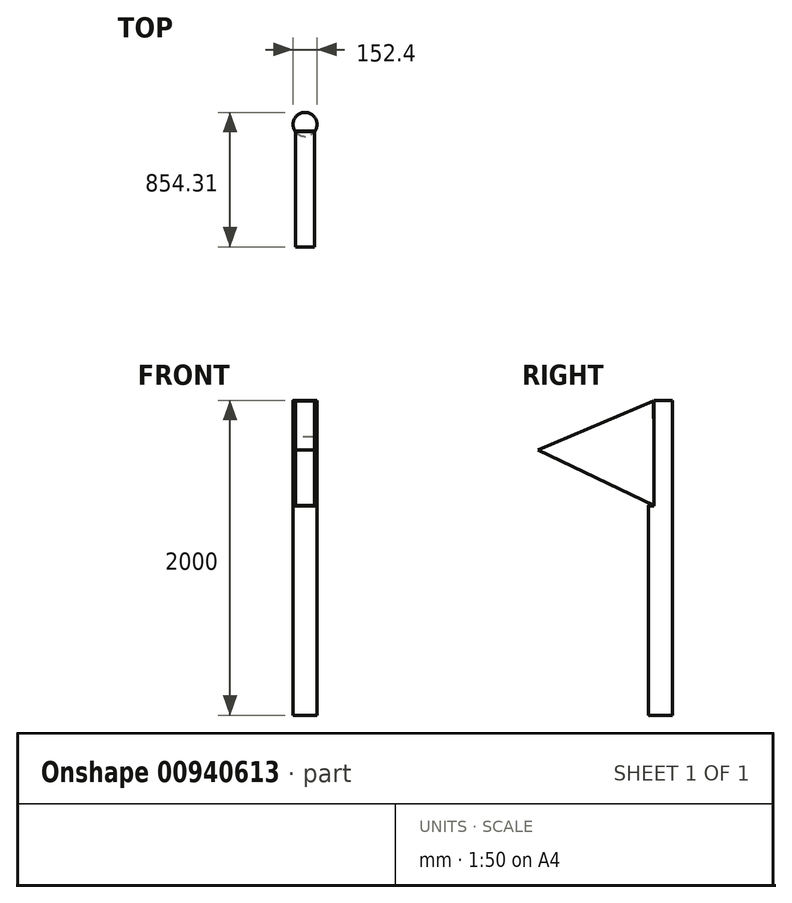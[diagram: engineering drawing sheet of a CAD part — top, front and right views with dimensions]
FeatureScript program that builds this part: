
annotation { "Feature Type Name" : "Feature", "Feature Type Description" : "" }
export const myFeature = defineFeature(function(context is Context, id is Id, definition is map)
    precondition{}
    {
        {
            var Q0;
            Q0=qCreatedBy(makeId("Top.planeOp"),FACE);
            var sketch = newSketch(context, id + "F0", { "sketchPlane" : qUnion([Q0])});
            skCircle(sketch, "E0", {"center": v(0, 0) * mm, "radius": 76.2 * mm});
            skSolve(sketch);
        }
        {
            var Q0;
            Q0=makeQuery(id+"F0.imprint","IMPRINT",FACE,{"disambiguationData":[TD([[makeQuery(id+"F0.imprint","IMPRINT",EDGE,{"derivedFrom":sQuery(id+"F0.wireOp",EDGE,"E0")}),1.0]])]});
            extrude(context, id + "F1", {"entities" : qUnion([Q0]), "depth" : 2000 * mm, "offsetDistance" : 25 * mm});
        }
        {
            var Q0;
            Q0=makeQuery(id+"F1.opExtrude","CAP_FACE",FACE,{"disambiguationData":[OSD([sQuery(id+"F0.wireOp",EDGE,"E0")])],"isStart":false});
            var sketch = newSketch(context, id + "F2", { "sketchPlane" : qUnion([Q0])});
            skLineSegment(sketch, "E1.bottom", {"start": v(-76.2, -42.65) * mm, "end": v(76.2, -42.65) * mm});
            skLineSegment(sketch, "E1.top", {"start": v(-76.2, -102.65) * mm, "end": v(76.2, -102.65) * mm});
            skLineSegment(sketch, "E1.left", {"start": v(-76.2, -42.65) * mm, "end": v(-76.2, -102.65) * mm});
            skLineSegment(sketch, "E1.right", {"start": v(76.2, -42.65) * mm, "end": v(76.2, -102.65) * mm});
            skPoint(sketch, "E1.middle", {"position": v(0, -72.65) * mm});
            skLineSegment(sketch, "E2", {"start": v(-76.2, 0) * mm, "end": v(-76.2, -112.65) * mm, "construction": true});
            skSolve(sketch);
        }
        {
            var Q0;
            Q0=makeQuery(id+"F2.imprint","IMPRINT",FACE,{"disambiguationData":[TD([[makeQuery(id+"F2.imprint","IMPRINT",EDGE,{"derivedFrom":sQuery(id+"F2.wireOp",EDGE,"E1.top")}),1.0]])]});
            var Q1;
            {var subQ0=sQuery(id+"F2.wireOp",EDGE,"E1.bottom");var subQ1=makeQuery(id+"F1.opExtrude","CAP_EDGE",EDGE,{"disambiguationData":[OSD([sQuery(id+"F0.wireOp",EDGE,"E0")])],"isStart":false});var subQ2=makeQuery(id+"F2.imprint","INTERSECT",VERTEX,{"disambiguationData":[OD(0.0)],"derivedFrom":[subQ1,subQ0]});Q1=makeQuery(id+"F2.imprint","IMPRINT",FACE,{"disambiguationData":[TD([[makeQuery(id+"F2.imprint","IMPRINT",EDGE,{"disambiguationData":[TD([[subQ2,-1.0]])],"derivedFrom":subQ0}),-1.0]])]});}
            extrude(context, id + "F3", {"entities" : qUnion([Q0, Q1]), "operationType" : NewBodyOperationType.REMOVE, "oppositeDirection" : true, "depth" : 670 * mm, "offsetDistance" : 25 * mm});
        }
        {
            var Q0;
            Q0=qCreatedBy(makeId("Right.planeOp"),FACE);
            var sketch = newSketch(context, id + "F4", { "sketchPlane" : qUnion([Q0])});
            skLineSegment(sketch, "E3", {"start": v(-45.17, 1995.65) * mm, "end": v(-778.1, 1684.87) * mm});
            skLineSegment(sketch, "E4", {"start": v(-778.1, 1684.87) * mm, "end": v(-37.8, 1330.95) * mm});
            skLineSegment(sketch, "E5", {"start": v(-45.17, 1995.65) * mm, "end": v(-37.8, 1330.95) * mm});
            skSolve(sketch);
        }
        {
            var Q0;
            Q0=makeQuery(id+"F4.imprint","IMPRINT",FACE,{"disambiguationData":[TD([[makeQuery(id+"F4.imprint","IMPRINT",EDGE,{"derivedFrom":sQuery(id+"F4.wireOp",EDGE,"E3")}),1.0]])]});
            extrude(context, id + "F5", {"entities" : qUnion([Q0]), "operationType" : NewBodyOperationType.ADD, "endBound" : BoundingType.SYMMETRIC, "depth" : 122 * mm, "offsetDistance" : 25 * mm});
        }
    });
